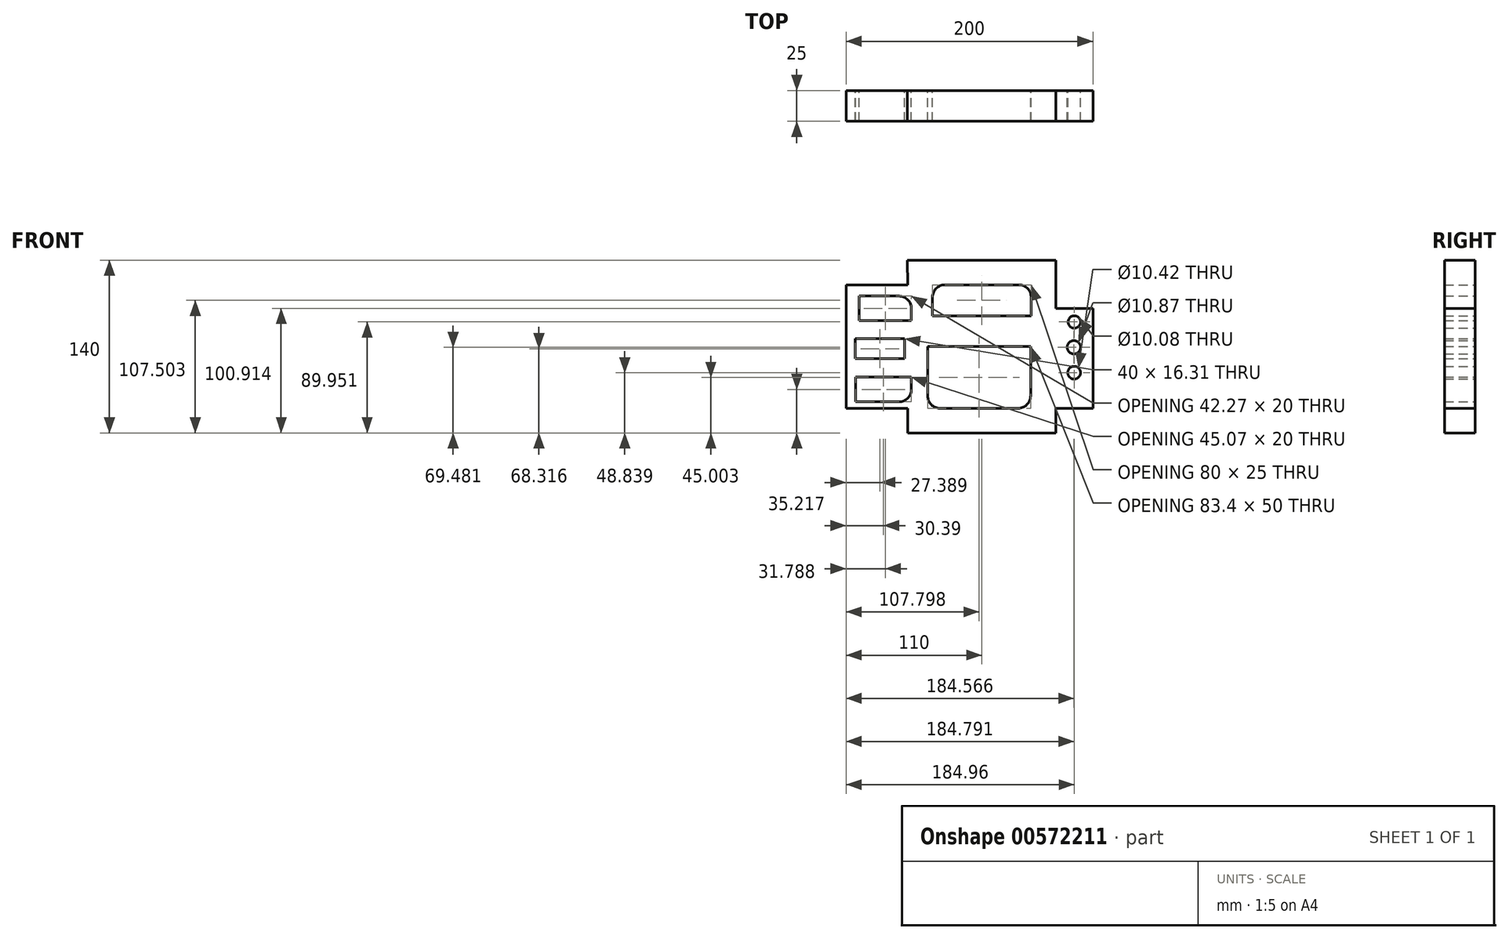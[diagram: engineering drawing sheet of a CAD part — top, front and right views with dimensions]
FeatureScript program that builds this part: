
annotation { "Feature Type Name" : "Feature", "Feature Type Description" : "" }
export const myFeature = defineFeature(function(context is Context, id is Id, definition is map)
    precondition{}
    {
        {
            var Q0;
            Q0=qCreatedBy(makeId("Front.planeOp"),FACE);
            var sketch = newSketch(context, id + "F0", { "sketchPlane" : qUnion([Q0])});
            skLineSegment(sketch, "E0", {"start": v(-120.47, 63.53) * mm, "end": v(0, 63.53) * mm});
            skLineSegment(sketch, "E1", {"start": v(0, 63.53) * mm, "end": v(0, 24.27) * mm});
            skLineSegment(sketch, "E2", {"start": v(0, 24.27) * mm, "end": v(30, 24.27) * mm});
            skLineSegment(sketch, "E3", {"start": v(30, 24.27) * mm, "end": v(30, -56.47) * mm});
            skLineSegment(sketch, "E4", {"start": v(30, -56.47) * mm, "end": v(0, -56.47) * mm});
            skLineSegment(sketch, "E5", {"start": v(0, -56.47) * mm, "end": v(0, -76.47) * mm});
            skLineSegment(sketch, "E6", {"start": v(0, -76.47) * mm, "end": v(-120, -76.47) * mm});
            skLineSegment(sketch, "E7", {"start": v(-120, -76.47) * mm, "end": v(-120, -56.47) * mm});
            skLineSegment(sketch, "E8", {"start": v(-120, -56.47) * mm, "end": v(-170, -56.47) * mm});
            skLineSegment(sketch, "E9", {"start": v(-170, -56.47) * mm, "end": v(-170, 43.53) * mm});
            skLineSegment(sketch, "E10", {"start": v(-170, 43.53) * mm, "end": v(-120, 43.53) * mm});
            skLineSegment(sketch, "E11", {"start": v(-120, 43.53) * mm, "end": v(-120.47, 63.53) * mm});
            skLineSegment(sketch, "E12.bottom", {"start": v(-162.61, 0) * mm, "end": v(-122.61, 0) * mm});
            skLineSegment(sketch, "E12.top", {"start": v(-162.61, -16.3) * mm, "end": v(-122.61, -16.3) * mm});
            skLineSegment(sketch, "E12.left", {"start": v(-162.61, 0) * mm, "end": v(-162.61, -16.3) * mm});
            skLineSegment(sketch, "E12.right", {"start": v(-122.61, 0) * mm, "end": v(-122.61, -16.3) * mm});
            skLineSegment(sketch, "E13.bottom", {"start": v(-159.35, 34.44) * mm, "end": v(-127.07, 34.44) * mm});
            skLineSegment(sketch, "E13.top", {"start": v(-159.35, 14.44) * mm, "end": v(-117.07, 14.44) * mm});
            skLineSegment(sketch, "E13.left", {"start": v(-159.35, 34.44) * mm, "end": v(-159.35, 14.44) * mm});
            skLineSegment(sketch, "E13.right", {"start": v(-117.07, 24.44) * mm, "end": v(-117.07, 14.44) * mm});
            skLineSegment(sketch, "E14.bottom", {"start": v(-162.15, -31.25) * mm, "end": v(-117.07, -31.25) * mm});
            skLineSegment(sketch, "E14.top", {"start": v(-162.15, -51.25) * mm, "end": v(-127.07, -51.25) * mm});
            skLineSegment(sketch, "E14.left", {"start": v(-162.15, -31.25) * mm, "end": v(-162.15, -51.25) * mm});
            skLineSegment(sketch, "E14.right", {"start": v(-117.07, -31.25) * mm, "end": v(-117.07, -41.25) * mm});
            skCircle(sketch, "E15", {"center": v(14.96, 13.48) * mm, "radius": 5.04 * mm});
            skCircle(sketch, "E16", {"center": v(14.57, -6.99) * mm, "radius": 5.43 * mm});
            skCircle(sketch, "E17", {"center": v(14.8, -27.63) * mm, "radius": 5.2 * mm});
            skLineSegment(sketch, "E18.bottom", {"start": v(-100, 18.53) * mm, "end": v(-20, 18.53) * mm});
            skLineSegment(sketch, "E18.top", {"start": v(-90, 43.53) * mm, "end": v(-30, 43.53) * mm});
            skLineSegment(sketch, "E18.left", {"start": v(-100, 18.53) * mm, "end": v(-100, 33.53) * mm});
            skLineSegment(sketch, "E18.right", {"start": v(-20, 18.53) * mm, "end": v(-20, 33.53) * mm});
            skLineSegment(sketch, "E19.bottom", {"start": v(-103.9, -6.47) * mm, "end": v(-20.5, -6.47) * mm});
            skLineSegment(sketch, "E19.top", {"start": v(-93.9, -56.47) * mm, "end": v(-30.5, -56.47) * mm});
            skLineSegment(sketch, "E19.left", {"start": v(-103.9, -6.47) * mm, "end": v(-103.9, -46.47) * mm});
            skLineSegment(sketch, "E19.right", {"start": v(-20.5, -6.47) * mm, "end": v(-20.5, -46.47) * mm});
            skPoint(sketch, "E20.visualSharp", {"position": v(-117.07, 34.44) * mm});
            skArc(sketch, "E20.filletArc", {"start": v(-117.07, 24.44) * mm, "mid": v(-120, 31.52) * mm, "end": v(-127.07, 34.44) * mm});
            skPoint(sketch, "E21.visualSharp", {"position": v(-117.07, -51.25) * mm});
            skArc(sketch, "E21.filletArc", {"start": v(-127.07, -51.25) * mm, "mid": v(-120, -48.32) * mm, "end": v(-117.07, -41.25) * mm});
            skPoint(sketch, "E22.visualSharp", {"position": v(-20.5, -56.47) * mm});
            skArc(sketch, "E22.filletArc", {"start": v(-30.5, -56.47) * mm, "mid": v(-23.43, -53.54) * mm, "end": v(-20.5, -46.47) * mm});
            skPoint(sketch, "E23.visualSharp", {"position": v(-103.9, -56.47) * mm});
            skArc(sketch, "E23.filletArc", {"start": v(-103.9, -46.47) * mm, "mid": v(-100.97, -53.54) * mm, "end": v(-93.9, -56.47) * mm});
            skPoint(sketch, "E24.visualSharp", {"position": v(-100, 43.53) * mm});
            skArc(sketch, "E24.filletArc", {"start": v(-90, 43.53) * mm, "mid": v(-97.07, 40.6) * mm, "end": v(-100, 33.53) * mm});
            skPoint(sketch, "E25.visualSharp", {"position": v(-20, 43.53) * mm});
            skArc(sketch, "E25.filletArc", {"start": v(-20, 33.53) * mm, "mid": v(-22.93, 40.6) * mm, "end": v(-30, 43.53) * mm});
            skSolve(sketch);
        }
        {
            var Q0;
            Q0 = qSketchRegion(id + "F0", true);
            extrude(context, id + "F1", {"entities" : qUnion([Q0]), "depth" : 25 * mm, "offsetDistance" : 25 * mm});
        }
    });
